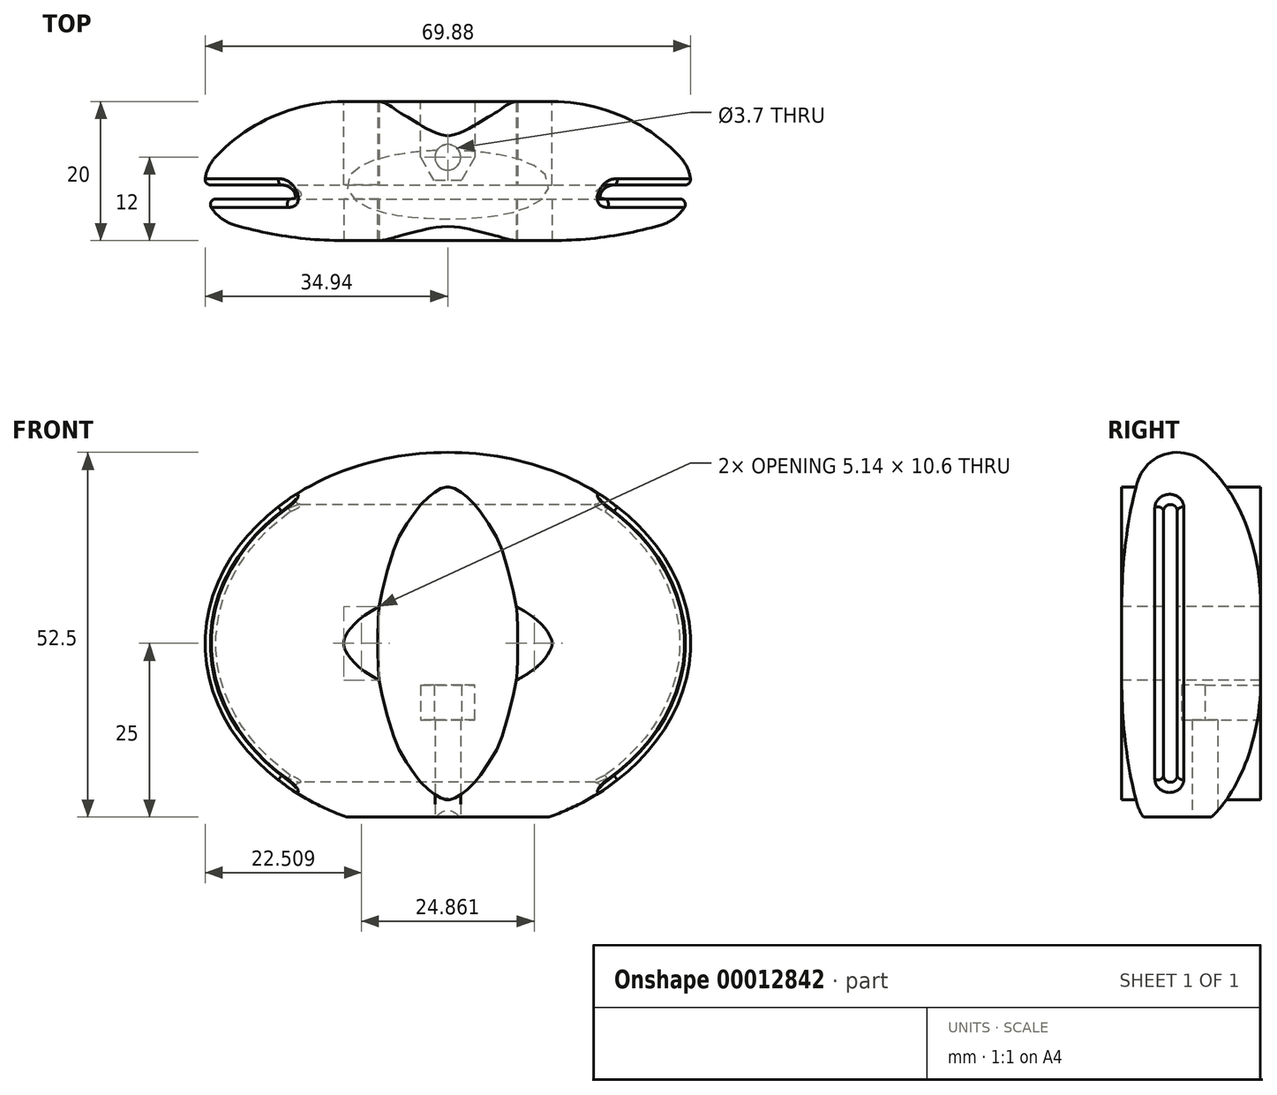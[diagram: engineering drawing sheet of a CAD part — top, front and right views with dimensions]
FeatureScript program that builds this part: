
annotation { "Feature Type Name" : "Feature", "Feature Type Description" : "" }
export const myFeature = defineFeature(function(context is Context, id is Id, definition is map)
    precondition{}
    {
        {
            var Q0;
            Q0=qCreatedBy(makeId("Front.planeOp"),FACE);
            var sketch = newSketch(context, id + "F0", { "sketchPlane" : qUnion([Q0])});
            skEllipse(sketch, "E0", {"center": v(0, 0) * mm, "majorRadius": 27.5 * mm, "minorRadius": 35 * mm, "majorAxis": v(0, 1)});
            skLineSegment(sketch, "E1", {"start": v(0, 0) * mm, "end": v(0, 27.5) * mm, "construction": true});
            skSolve(sketch);
        }
        {
            var Q0;
            Q0=qCreatedBy(makeId("Right.planeOp"),FACE);
            var sketch = newSketch(context, id + "F1", { "sketchPlane" : qUnion([Q0])});
            skCircle(sketch, "E2", {"center": v(0, 21.5) * mm, "radius": 6 * mm, "construction": true});
            skArc(sketch, "E3", {"start": v(-5.76, 23.18) * mm, "mid": v(-7.44, 15.42) * mm, "end": v(-8, 7.5) * mm});
            skArc(sketch, "E4", {"start": v(12, 7.5) * mm, "mid": v(9.95, 17.48) * mm, "end": v(4.14, 25.84) * mm});
            skLineSegment(sketch, "E5", {"start": v(-8, 7.5) * mm, "end": v(12, 7.5) * mm});
            skLineSegment(sketch, "E6", {"start": v(12, 16.14) * mm, "end": v(12, 7.5) * mm, "construction": true});
            skLineSegment(sketch, "E7", {"start": v(-8, 53.87) * mm, "end": v(-8, 7.5) * mm, "construction": true});
            skArc(sketch, "E8", {"start": v(4.14, 25.84) * mm, "mid": v(-1.56, 27.3) * mm, "end": v(-5.76, 23.18) * mm});
            skLineSegment(sketch, "E9", {"start": v(0, 21.5) * mm, "end": v(0, 7.5) * mm, "construction": true});
            skLineSegment(sketch, "E10", {"start": v(0, 21.5) * mm, "end": v(0, 27.5) * mm, "construction": true});
            skSolve(sketch);
        }
        {
            var Q0;
            Q0=makeQuery(id+"F1.imprint","IMPRINT",FACE,{"disambiguationData":[TD([[makeQuery(id+"F1.imprint","IMPRINT",EDGE,{"derivedFrom":sQuery(id+"F1.wireOp",EDGE,"E3")}),1.0]])]});
            var Q1;
            Q1=sQuery(id+"F0.wireOp",EDGE,"E0");
            sweep(context, id + "F2", {"profiles" : qUnion([Q0]), "path" : qUnion([Q1])});
        }
        {
            var Q0;
            Q0=qCreatedBy(makeId("Front.planeOp"),FACE);
            var sketch = newSketch(context, id + "F3", { "sketchPlane" : qUnion([Q0])});
            skFitSpline(sketch, "E11.0", {"points": [v(0, 22.5) * mm, v(-0.16, 22.5) * mm, v(-0.33, 22.48) * mm, v(-0.85, 22.33) * mm, v(-1.2, 22.19) * mm, v(-2.1, 21.62) * mm, v(-2.66, 21.2) * mm, v(-3.88, 19.97) * mm, v(-4.54, 19.18) * mm, v(-6.5, 16.23) * mm, v(-7.77, 13.52) * mm, v(-9.51, 7.2) * mm, v(-10, 3.6) * mm, v(-10, -3.6) * mm, v(-9.51, -7.2) * mm, v(-7.77, -13.52) * mm, v(-6.5, -16.23) * mm, v(-4.54, -19.18) * mm, v(-3.88, -19.97) * mm, v(-2.66, -21.2) * mm, v(-2.1, -21.62) * mm, v(-1.2, -22.19) * mm, v(-0.85, -22.33) * mm, v(-0.33, -22.48) * mm, v(-0.16, -22.5) * mm, v(0.16, -22.5) * mm, v(0.33, -22.48) * mm, v(0.85, -22.33) * mm, v(1.2, -22.19) * mm, v(2.1, -21.62) * mm, v(2.66, -21.2) * mm, v(3.88, -19.97) * mm, v(4.54, -19.18) * mm, v(6.5, -16.23) * mm, v(7.77, -13.52) * mm, v(9.51, -7.2) * mm, v(10, -3.6) * mm, v(10, 3.6) * mm, v(9.51, 7.2) * mm, v(7.77, 13.52) * mm, v(6.5, 16.23) * mm, v(4.54, 19.18) * mm, v(3.88, 19.97) * mm, v(2.66, 21.2) * mm, v(2.1, 21.62) * mm, v(1.2, 22.19) * mm, v(0.85, 22.33) * mm, v(0.33, 22.48) * mm, v(0.16, 22.5) * mm, v(0, 22.5) * mm]});
            skSolve(sketch);
        }
        {
            var Q0;
            Q0 = qSketchRegion(id + "F3", true);
            var Q1;
            Q1=makeQuery(id+"F2.opSweep","SWEPT_FACE",FACE,{"disambiguationData":[OSD([sQuery(id+"F0.wireOp",EDGE,"E0"),sQuery(id+"F1.wireOp",EDGE,"E3")])]});
            extrude(context, id + "F4", {"entities" : qUnion([Q0]), "operationType" : NewBodyOperationType.ADD, "endBoundEntity" : qUnion([Q1]), "depth" : 8 * mm, "hasSecondDirection" : true, "secondDirectionOppositeDirection" : true, "secondDirectionDepth" : 12 * mm});
        }
        {
            var Q0;
            Q0=qCreatedBy(makeId("Right.planeOp"),FACE);
            var sketch = newSketch(context, id + "F5", { "sketchPlane" : qUnion([Q0])});
            skLineSegment(sketch, "E12.bottom", {"start": v(-2, 20) * mm, "end": v(0, 20) * mm});
            skLineSegment(sketch, "E12.top", {"start": v(-2, -20) * mm, "end": v(0, -20) * mm});
            skLineSegment(sketch, "E12.left", {"start": v(0, 20) * mm, "end": v(0, -20) * mm});
            skLineSegment(sketch, "E12.right", {"start": v(-2, 20) * mm, "end": v(-2, -20) * mm});
            skSolve(sketch);
        }
        {
            var Q0;
            Q0 = qSketchRegion(id + "F5", true);
            extrude(context, id + "F6", {"entities" : qUnion([Q0]), "operationType" : NewBodyOperationType.REMOVE, "endBound" : BoundingType.THROUGH_ALL, "oppositeDirection" : true, "depth" : 25 * mm, "hasSecondDirection" : true, "secondDirectionBound" : SecondDirectionBoundingType.THROUGH_ALL, "secondDirectionOppositeDirection" : false, "secondDirectionDepth" : 25 * mm});
        }
        {
            var Q0;
            Q0=makeQuery(id+"F6.boolean.opBoolean","COPY",EDGE,{"derivedFrom":makeQuery(id+"F6.opExtrude","SWEPT_EDGE",EDGE,{"disambiguationData":[OSD([sQuery(id+"F5.wireOp",EDGE,"E12.bottom"),sQuery(id+"F5.wireOp",EDGE,"E12.right")])]})});
            var Q1;
            Q1=makeQuery(id+"F6.boolean.opBoolean","COPY",EDGE,{"derivedFrom":makeQuery(id+"F6.opExtrude","SWEPT_EDGE",EDGE,{"disambiguationData":[OSD([sQuery(id+"F5.wireOp",EDGE,"E12.bottom"),sQuery(id+"F5.wireOp",EDGE,"E12.left")])]})});
            var Q2;
            Q2=makeQuery(id+"F6.boolean.opBoolean","COPY",EDGE,{"derivedFrom":makeQuery(id+"F6.opExtrude","SWEPT_EDGE",EDGE,{"disambiguationData":[OSD([sQuery(id+"F5.wireOp",EDGE,"E12.top"),sQuery(id+"F5.wireOp",EDGE,"E12.right")])]})});
            var Q3;
            Q3=makeQuery(id+"F6.boolean.opBoolean","COPY",EDGE,{"derivedFrom":makeQuery(id+"F6.opExtrude","SWEPT_EDGE",EDGE,{"disambiguationData":[OSD([sQuery(id+"F5.wireOp",EDGE,"E12.top"),sQuery(id+"F5.wireOp",EDGE,"E12.left")])]})});
            fillet(context, id + "F7", {"entities" : qUnion([Q0, Q1, Q2, Q3]), "radius" : 1 * mm, "tangentPropagation" : true, "allowEdgeOverflow" : false});
        }
        {
            var Q0;
            Q0=qCreatedBy(makeId("Right.planeOp"),FACE);
            var sketch = newSketch(context, id + "F8", { "sketchPlane" : qUnion([Q0])});
            skLineSegment(sketch, "E13", {"start": v(-9.7, -25) * mm, "end": v(12.72, -25) * mm});
            skLineSegment(sketch, "E14", {"start": v(12.72, -25) * mm, "end": v(14.86, -55.14) * mm});
            skLineSegment(sketch, "E15", {"start": v(14.86, -55.14) * mm, "end": v(-15.13, -48.74) * mm});
            skLineSegment(sketch, "E16", {"start": v(-15.13, -48.74) * mm, "end": v(-9.7, -25) * mm});
            skLineSegment(sketch, "E17", {"start": v(0, 0) * mm, "end": v(0, -25) * mm, "construction": true});
            skSolve(sketch);
        }
        {
            var Q0;
            Q0 = qSketchRegion(id + "F8", true);
            extrude(context, id + "F9", {"entities" : qUnion([Q0]), "operationType" : NewBodyOperationType.REMOVE, "endBound" : BoundingType.THROUGH_ALL, "oppositeDirection" : true, "depth" : 25 * mm, "hasSecondDirection" : true, "secondDirectionBound" : SecondDirectionBoundingType.THROUGH_ALL, "secondDirectionOppositeDirection" : false, "secondDirectionDepth" : 25 * mm});
        }
        {
            var Q0;
            Q0=makeQuery(id+"F9.boolean.opBoolean","COPY",FACE,{"derivedFrom":makeQuery(id+"F9.opExtrude","SWEPT_FACE",FACE,{"disambiguationData":[OSD([sQuery(id+"F8.wireOp",EDGE,"E13")])]})});
            var sketch = newSketch(context, id + "F10", { "sketchPlane" : qUnion([Q0])});
            skCircle(sketch, "E18", {"center": v(0, -4) * mm, "radius": 1.85 * mm});
            skLineSegment(sketch, "E19", {"start": v(0, 0) * mm, "end": v(0, -4) * mm, "construction": true});
            skSolve(sketch);
        }
        {
            var Q0;
            Q0 = qSketchRegion(id + "F10", true);
            extrude(context, id + "F11", {"entities" : qUnion([Q0]), "operationType" : NewBodyOperationType.REMOVE, "oppositeDirection" : true, "depth" : 14 * mm});
        }
        {
            var Q0;
            Q0=makeQuery(id+"F6.boolean.opBoolean","INTERSECT",EDGE,{"disambiguationData":[OD(1.0)],"derivedFrom":[makeQuery(id+"F2.opSweep","SWEPT_FACE",FACE,{"disambiguationData":[OSD([sQuery(id+"F0.wireOp",EDGE,"E0"),sQuery(id+"F1.wireOp",EDGE,"E8")])]}),makeQuery(id+"F6.opExtrude","SWEPT_FACE",FACE,{"disambiguationData":[OSD([sQuery(id+"F5.wireOp",EDGE,"E12.left")])]})]});
            var Q1;
            Q1=makeQuery(id+"F6.boolean.opBoolean","INTERSECT",EDGE,{"disambiguationData":[OD(0.0)],"derivedFrom":[makeQuery(id+"F2.opSweep","SWEPT_FACE",FACE,{"disambiguationData":[OSD([sQuery(id+"F0.wireOp",EDGE,"E0"),sQuery(id+"F1.wireOp",EDGE,"E8")])]}),makeQuery(id+"F6.opExtrude","SWEPT_FACE",FACE,{"disambiguationData":[OSD([sQuery(id+"F5.wireOp",EDGE,"E12.left")])]})]});
            fillet(context, id + "F12", {"entities" : qUnion([Q0, Q1]), "radius" : .8 * mm, "tangentPropagation" : true, "allowEdgeOverflow" : false});
        }
        {
            var Q0;
            Q0=makeQuery(id+"F11.boolean.opBoolean","COPY",FACE,{"derivedFrom":makeQuery(id+"F11.opExtrude","CAP_FACE",FACE,{"disambiguationData":[OSD([sQuery(id+"F10.wireOp",EDGE,"E18")])],"isStart":false})});
            var sketch = newSketch(context, id + "F13", { "sketchPlane" : qUnion([Q0])});
            skLineSegment(sketch, "E20", {"start": v(1.95, -0.62) * mm, "end": v(-1.95, -0.62) * mm});
            skLineSegment(sketch, "E21", {"start": v(-1.95, -0.62) * mm, "end": v(-3.9, -4) * mm});
            skLineSegment(sketch, "E22", {"start": v(-3.9, -4) * mm, "end": v(-3.9, -13.51) * mm});
            skLineSegment(sketch, "E23", {"start": v(-3.9, -13.51) * mm, "end": v(3.9, -13.51) * mm});
            skLineSegment(sketch, "E24", {"start": v(3.9, -13.51) * mm, "end": v(3.9, -4) * mm});
            skLineSegment(sketch, "E25", {"start": v(3.9, -4) * mm, "end": v(1.95, -0.62) * mm});
            skCircle(sketch, "E26", {"center": v(0, -4) * mm, "radius": 3.9 * mm, "construction": true});
            skSolve(sketch);
        }
        {
            var Q0;
            Q0 = qSketchRegion(id + "F13", true);
            extrude(context, id + "F14", {"entities" : qUnion([Q0]), "operationType" : NewBodyOperationType.REMOVE, "oppositeDirection" : true, "depth" : 5 * mm});
        }
    });
